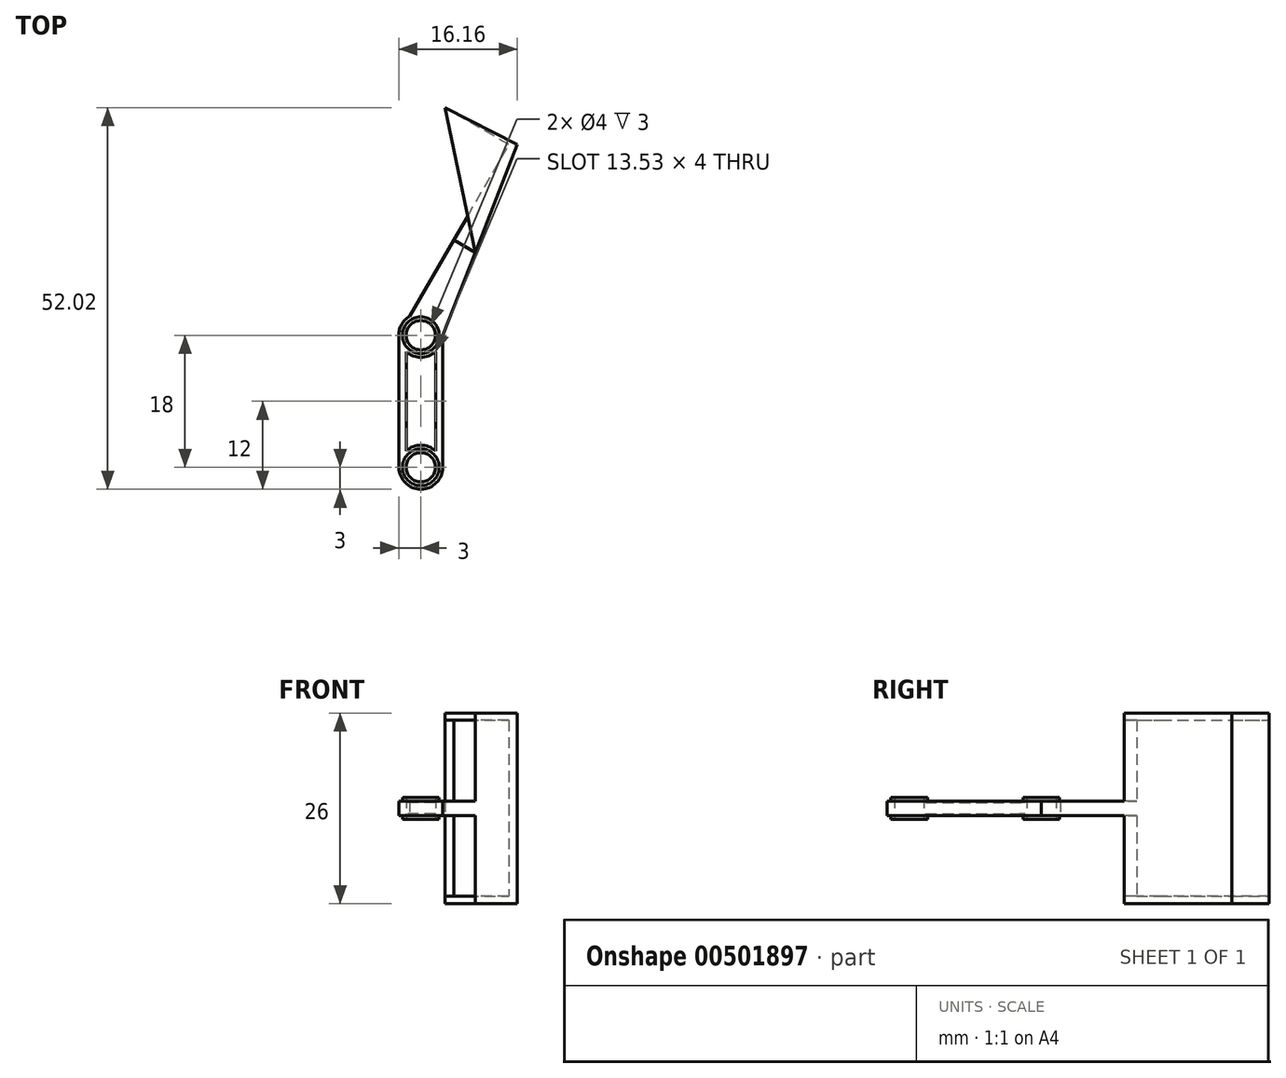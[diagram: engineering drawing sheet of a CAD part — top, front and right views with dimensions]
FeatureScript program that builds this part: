
annotation { "Feature Type Name" : "Feature", "Feature Type Description" : "" }
export const myFeature = defineFeature(function(context is Context, id is Id, definition is map)
    precondition{}
    {
        {
            var Q0;
            Q0=qCreatedBy(makeId("Front.planeOp"),FACE);
            var sketch = newSketch(context, id + "F0", { "sketchPlane" : qUnion([Q0])});
            skLineSegment(sketch, "E0.left", {"start": v(3, -1) * mm, "end": v(3, 1) * mm});
            skLineSegment(sketch, "E0.right", {"start": v(-3, -1) * mm, "end": v(-3, 1) * mm});
            skPoint(sketch, "E0.middle", {"position": v(0, 0) * mm});
            skLineSegment(sketch, "E1", {"start": v(-3, 1) * mm, "end": v(-2, 1) * mm});
            skLineSegment(sketch, "E2", {"start": v(-2, 1) * mm, "end": v(-2, 0.75) * mm});
            skLineSegment(sketch, "E3", {"start": v(-2, 0.75) * mm, "end": v(2, 0.75) * mm});
            skLineSegment(sketch, "E4", {"start": v(2, 0.75) * mm, "end": v(2, 1) * mm});
            skLineSegment(sketch, "E5", {"start": v(2, 1) * mm, "end": v(3, 1) * mm});
            skLineSegment(sketch, "E6", {"start": v(-3, -1) * mm, "end": v(-2, -1) * mm});
            skLineSegment(sketch, "E7", {"start": v(-2, -1) * mm, "end": v(-2, -0.75) * mm});
            skLineSegment(sketch, "E8", {"start": v(-2, -0.75) * mm, "end": v(2, -0.75) * mm});
            skLineSegment(sketch, "E9", {"start": v(2, -0.75) * mm, "end": v(2, -1) * mm});
            skLineSegment(sketch, "E10", {"start": v(2, -1) * mm, "end": v(3, -1) * mm});
            skSolve(sketch);
        }
        {
            var Q0;
            Q0=makeQuery(id+"F0.imprint","IMPRINT",FACE,{"disambiguationData":[TD([[makeQuery(id+"F0.imprint","IMPRINT",EDGE,{"derivedFrom":sQuery(id+"F0.wireOp",EDGE,"E0.left")}),1.0]])]});
            extrude(context, id + "F1", {"entities" : qUnion([Q0]), "endBound" : BoundingType.SYMMETRIC, "depth" : 18 * mm});
        }
        {
            var Q0;
            Q0=makeQuery(id+"F1.opExtrude","SWEPT_FACE",FACE,{"disambiguationData":[OSD([sQuery(id+"F0.wireOp",EDGE,"E8")])]});
            var sketch = newSketch(context, id + "F2", { "sketchPlane" : qUnion([Q0])});
            skCircle(sketch, "E11", {"center": v(0, 9) * mm, "radius": 2 * mm});
            skCircle(sketch, "E12", {"center": v(0, 9) * mm, "radius": 3 * mm});
            skCircle(sketch, "E13", {"center": v(0, -9) * mm, "radius": 2 * mm});
            skPoint(sketch, "E13.centerSnap0", {"position": v(0, -9) * mm});
            skCircle(sketch, "E14", {"center": v(0, -9) * mm, "radius": 3 * mm});
            skSolve(sketch);
        }
        {
            var Q0;
            {var subQ1=sQuery(id+"F0.wireOp",EDGE,"E8");var subQ2=makeQuery(id+"F1.opExtrude","CAP_EDGE",EDGE,{"disambiguationData":[OSD([subQ1])],"isStart":false});Q0=makeQuery(id+"F2.imprint","IMPRINT",FACE,{"disambiguationData":[TD([[makeQuery(id+"F2.imprint","IMPRINT",EDGE,{"derivedFrom":subQ2}),-1.0]])]});}
            extrude(context, id + "F3", {"entities" : qUnion([Q0]), "operationType" : NewBodyOperationType.REMOVE, "oppositeDirection" : true, "depth" : 2 * mm});
        }
        {
            var Q0;
            {var subQ1=sQuery(id+"F0.wireOp",EDGE,"E8");var subQ2=makeQuery(id+"F1.opExtrude","CAP_EDGE",EDGE,{"disambiguationData":[OSD([subQ1])],"isStart":true});Q0=makeQuery(id+"F2.imprint","IMPRINT",FACE,{"disambiguationData":[TD([[makeQuery(id+"F2.imprint","IMPRINT",EDGE,{"derivedFrom":subQ2}),1.0]])]});}
            extrude(context, id + "F4", {"entities" : qUnion([Q0]), "operationType" : NewBodyOperationType.REMOVE, "oppositeDirection" : true, "depth" : 2 * mm});
        }
        {
            var Q0;
            {var subQ1=sQuery(id+"F0.wireOp",EDGE,"E8");var subQ3=makeQuery(id+"F1.opExtrude","SWEPT_EDGE",EDGE,{"disambiguationData":[OSD([sQuery(id+"F0.wireOp",EDGE,"E7"),subQ1])]});var subQ7=sQuery(id+"F2.wireOp",EDGE,"E14");var subQ8=makeQuery(id+"F2.imprint","INTERSECT",VERTEX,{"derivedFrom":[subQ3,subQ7]});Q0=makeQuery(id+"F2.imprint","IMPRINT",FACE,{"disambiguationData":[TD([[makeQuery(id+"F2.imprint","IMPRINT",EDGE,{"disambiguationData":[TD([[subQ8,-1.0]])],"derivedFrom":subQ7}),1.0]])]});}
            var Q1;
            {var subQ1=sQuery(id+"F0.wireOp",EDGE,"E8");var subQ3=makeQuery(id+"F1.opExtrude","SWEPT_EDGE",EDGE,{"disambiguationData":[OSD([sQuery(id+"F0.wireOp",EDGE,"E7"),subQ1])]});var subQ7=sQuery(id+"F2.wireOp",EDGE,"E14");var subQ8=makeQuery(id+"F2.imprint","INTERSECT",VERTEX,{"derivedFrom":[subQ3,subQ7]});Q1=makeQuery(id+"F2.imprint","IMPRINT",FACE,{"disambiguationData":[TD([[makeQuery(id+"F2.imprint","IMPRINT",EDGE,{"disambiguationData":[TD([[subQ8,1.0]])],"derivedFrom":subQ7}),1.0]])]});}
            extrude(context, id + "F5", {"entities" : qUnion([Q0, Q1]), "operationType" : NewBodyOperationType.REMOVE, "oppositeDirection" : true, "depth" : 2 * mm});
        }
        {
            var Q0;
            {var subQ1=sQuery(id+"F0.wireOp",EDGE,"E8");var subQ3=makeQuery(id+"F1.opExtrude","SWEPT_EDGE",EDGE,{"disambiguationData":[OSD([sQuery(id+"F0.wireOp",EDGE,"E7"),subQ1])]});var subQ7=sQuery(id+"F2.wireOp",EDGE,"E14");var subQ8=makeQuery(id+"F2.imprint","INTERSECT",VERTEX,{"derivedFrom":[subQ3,subQ7]});Q0=makeQuery(id+"F2.imprint","IMPRINT",FACE,{"disambiguationData":[TD([[makeQuery(id+"F2.imprint","IMPRINT",EDGE,{"disambiguationData":[TD([[subQ8,-1.0]])],"derivedFrom":subQ7}),1.0]])]});}
            extrude(context, id + "F6", {"entities" : qUnion([Q0]), "operationType" : NewBodyOperationType.REMOVE, "oppositeDirection" : true, "depth" : 25 * mm});
        }
        {
            var Q0;
            {var subQ1=sQuery(id+"F0.wireOp",EDGE,"E8");var subQ3=makeQuery(id+"F1.opExtrude","SWEPT_EDGE",EDGE,{"disambiguationData":[OSD([sQuery(id+"F0.wireOp",EDGE,"E7"),subQ1])]});var subQ7=sQuery(id+"F2.wireOp",EDGE,"E14");var subQ8=makeQuery(id+"F2.imprint","INTERSECT",VERTEX,{"derivedFrom":[subQ3,subQ7]});Q0=makeQuery(id+"F2.imprint","IMPRINT",FACE,{"disambiguationData":[TD([[makeQuery(id+"F2.imprint","IMPRINT",EDGE,{"disambiguationData":[TD([[subQ8,-1.0]])],"derivedFrom":subQ7}),1.0]])]});}
            extrude(context, id + "F7", {"entities" : qUnion([Q0]), "operationType" : NewBodyOperationType.REMOVE, "oppositeDirection" : true, "depth" : 25 * mm});
        }
        {
            var Q0;
            {var subQ1=sQuery(id+"F0.wireOp",EDGE,"E8");var subQ3=makeQuery(id+"F1.opExtrude","SWEPT_EDGE",EDGE,{"disambiguationData":[OSD([sQuery(id+"F0.wireOp",EDGE,"E7"),subQ1])]});var subQ7=sQuery(id+"F2.wireOp",EDGE,"E14");var subQ8=makeQuery(id+"F2.imprint","INTERSECT",VERTEX,{"derivedFrom":[subQ3,subQ7]});Q0=makeQuery(id+"F2.imprint","IMPRINT",FACE,{"disambiguationData":[TD([[makeQuery(id+"F2.imprint","IMPRINT",EDGE,{"disambiguationData":[TD([[subQ8,-1.0]])],"derivedFrom":subQ7}),1.0]])]});}
            extrude(context, id + "F8", {"entities" : qUnion([Q0]), "operationType" : NewBodyOperationType.REMOVE, "oppositeDirection" : true, "depth" : 25 * mm});
        }
        {
            var Q0;
            {var subQ1=sQuery(id+"F0.wireOp",EDGE,"E8");var subQ3=makeQuery(id+"F1.opExtrude","SWEPT_EDGE",EDGE,{"disambiguationData":[OSD([sQuery(id+"F0.wireOp",EDGE,"E7"),subQ1])]});var subQ7=sQuery(id+"F2.wireOp",EDGE,"E14");var subQ8=makeQuery(id+"F2.imprint","INTERSECT",VERTEX,{"derivedFrom":[subQ3,subQ7]});Q0=makeQuery(id+"F2.imprint","IMPRINT",FACE,{"disambiguationData":[TD([[makeQuery(id+"F2.imprint","IMPRINT",EDGE,{"disambiguationData":[TD([[subQ8,-1.0]])],"derivedFrom":subQ7}),1.0]])]});}
            extrude(context, id + "F9", {"entities" : qUnion([Q0]), "operationType" : NewBodyOperationType.REMOVE, "depth" : 2 * mm});
        }
        {
            var Q0;
            {var subQ1=sQuery(id+"F0.wireOp",EDGE,"E8");var subQ3=makeQuery(id+"F1.opExtrude","SWEPT_EDGE",EDGE,{"disambiguationData":[OSD([sQuery(id+"F0.wireOp",EDGE,"E7"),subQ1])]});var subQ7=sQuery(id+"F2.wireOp",EDGE,"E12");var subQ8=makeQuery(id+"F2.imprint","INTERSECT",VERTEX,{"derivedFrom":[subQ3,subQ7]});Q0=makeQuery(id+"F2.imprint","IMPRINT",FACE,{"disambiguationData":[TD([[makeQuery(id+"F2.imprint","IMPRINT",EDGE,{"disambiguationData":[TD([[subQ8,1.0]])],"derivedFrom":subQ7}),1.0]])]});}
            var Q1;
            {var subQ1=sQuery(id+"F0.wireOp",EDGE,"E8");var subQ3=makeQuery(id+"F1.opExtrude","SWEPT_EDGE",EDGE,{"disambiguationData":[OSD([sQuery(id+"F0.wireOp",EDGE,"E7"),subQ1])]});var subQ7=sQuery(id+"F2.wireOp",EDGE,"E12");var subQ8=makeQuery(id+"F2.imprint","INTERSECT",VERTEX,{"derivedFrom":[subQ3,subQ7]});Q1=makeQuery(id+"F2.imprint","IMPRINT",FACE,{"disambiguationData":[TD([[makeQuery(id+"F2.imprint","IMPRINT",EDGE,{"disambiguationData":[TD([[subQ8,-1.0]])],"derivedFrom":subQ7}),1.0]])]});}
            extrude(context, id + "F10", {"entities" : qUnion([Q0, Q1]), "operationType" : NewBodyOperationType.REMOVE, "oppositeDirection" : true, "depth" : 2 * mm});
        }
        {
            var Q0;
            {var subQ1=sQuery(id+"F0.wireOp",EDGE,"E8");var subQ3=makeQuery(id+"F1.opExtrude","SWEPT_EDGE",EDGE,{"disambiguationData":[OSD([sQuery(id+"F0.wireOp",EDGE,"E7"),subQ1])]});var subQ7=sQuery(id+"F2.wireOp",EDGE,"E12");var subQ8=makeQuery(id+"F2.imprint","INTERSECT",VERTEX,{"derivedFrom":[subQ3,subQ7]});Q0=makeQuery(id+"F2.imprint","IMPRINT",FACE,{"disambiguationData":[TD([[makeQuery(id+"F2.imprint","IMPRINT",EDGE,{"disambiguationData":[TD([[subQ8,1.0]])],"derivedFrom":subQ7}),1.0]])]});}
            extrude(context, id + "F11", {"entities" : qUnion([Q0]), "operationType" : NewBodyOperationType.REMOVE, "depth" : 2 * mm});
        }
        {
            var Q0;
            {var subQ1=sQuery(id+"F0.wireOp",EDGE,"E8");var subQ3=makeQuery(id+"F1.opExtrude","SWEPT_EDGE",EDGE,{"disambiguationData":[OSD([sQuery(id+"F0.wireOp",EDGE,"E7"),subQ1])]});var subQ7=sQuery(id+"F2.wireOp",EDGE,"E14");var subQ8=makeQuery(id+"F2.imprint","INTERSECT",VERTEX,{"derivedFrom":[subQ3,subQ7]});Q0=makeQuery(id+"F2.imprint","IMPRINT",FACE,{"disambiguationData":[TD([[makeQuery(id+"F2.imprint","IMPRINT",EDGE,{"disambiguationData":[TD([[subQ8,1.0]])],"derivedFrom":subQ7}),1.0]])]});}
            var Q1;
            {var subQ1=sQuery(id+"F0.wireOp",EDGE,"E8");var subQ3=makeQuery(id+"F1.opExtrude","SWEPT_EDGE",EDGE,{"disambiguationData":[OSD([sQuery(id+"F0.wireOp",EDGE,"E7"),subQ1])]});var subQ7=sQuery(id+"F2.wireOp",EDGE,"E14");var subQ8=makeQuery(id+"F2.imprint","INTERSECT",VERTEX,{"derivedFrom":[subQ3,subQ7]});Q1=makeQuery(id+"F2.imprint","IMPRINT",FACE,{"disambiguationData":[TD([[makeQuery(id+"F2.imprint","IMPRINT",EDGE,{"disambiguationData":[TD([[subQ8,-1.0]])],"derivedFrom":subQ7}),1.0]])]});}
            var Q2;
            {var subQ1=sQuery(id+"F0.wireOp",EDGE,"E8");var subQ3=makeQuery(id+"F1.opExtrude","SWEPT_EDGE",EDGE,{"disambiguationData":[OSD([sQuery(id+"F0.wireOp",EDGE,"E7"),subQ1])]});var subQ7=sQuery(id+"F2.wireOp",EDGE,"E12");var subQ8=makeQuery(id+"F2.imprint","INTERSECT",VERTEX,{"derivedFrom":[subQ3,subQ7]});Q2=makeQuery(id+"F2.imprint","IMPRINT",FACE,{"disambiguationData":[TD([[makeQuery(id+"F2.imprint","IMPRINT",EDGE,{"disambiguationData":[TD([[subQ8,-1.0]])],"derivedFrom":subQ7}),1.0]])]});}
            var Q3;
            {var subQ1=sQuery(id+"F0.wireOp",EDGE,"E8");var subQ3=makeQuery(id+"F1.opExtrude","SWEPT_EDGE",EDGE,{"disambiguationData":[OSD([sQuery(id+"F0.wireOp",EDGE,"E7"),subQ1])]});var subQ7=sQuery(id+"F2.wireOp",EDGE,"E12");var subQ8=makeQuery(id+"F2.imprint","INTERSECT",VERTEX,{"derivedFrom":[subQ3,subQ7]});Q3=makeQuery(id+"F2.imprint","IMPRINT",FACE,{"disambiguationData":[TD([[makeQuery(id+"F2.imprint","IMPRINT",EDGE,{"disambiguationData":[TD([[subQ8,1.0]])],"derivedFrom":subQ7}),1.0]])]});}
            extrude(context, id + "F12", {"entities" : qUnion([Q0, Q1, Q2, Q3]), "operationType" : NewBodyOperationType.ADD, "oppositeDirection" : true, "depth" : 1.75 * mm});
        }
        {
            var Q0;
            {var subQ1=sQuery(id+"F0.wireOp",EDGE,"E8");var subQ3=makeQuery(id+"F1.opExtrude","SWEPT_EDGE",EDGE,{"disambiguationData":[OSD([sQuery(id+"F0.wireOp",EDGE,"E7"),subQ1])]});var subQ7=sQuery(id+"F2.wireOp",EDGE,"E14");var subQ8=makeQuery(id+"F2.imprint","INTERSECT",VERTEX,{"derivedFrom":[subQ3,subQ7]});Q0=makeQuery(id+"F2.imprint","IMPRINT",FACE,{"disambiguationData":[TD([[makeQuery(id+"F2.imprint","IMPRINT",EDGE,{"disambiguationData":[TD([[subQ8,1.0]])],"derivedFrom":subQ7}),1.0]])]});}
            var Q1;
            {var subQ1=sQuery(id+"F0.wireOp",EDGE,"E8");var subQ3=makeQuery(id+"F1.opExtrude","SWEPT_EDGE",EDGE,{"disambiguationData":[OSD([sQuery(id+"F0.wireOp",EDGE,"E7"),subQ1])]});var subQ7=sQuery(id+"F2.wireOp",EDGE,"E14");var subQ8=makeQuery(id+"F2.imprint","INTERSECT",VERTEX,{"derivedFrom":[subQ3,subQ7]});Q1=makeQuery(id+"F2.imprint","IMPRINT",FACE,{"disambiguationData":[TD([[makeQuery(id+"F2.imprint","IMPRINT",EDGE,{"disambiguationData":[TD([[subQ8,-1.0]])],"derivedFrom":subQ7}),1.0]])]});}
            var Q2;
            {var subQ1=sQuery(id+"F0.wireOp",EDGE,"E8");var subQ3=makeQuery(id+"F1.opExtrude","SWEPT_EDGE",EDGE,{"disambiguationData":[OSD([sQuery(id+"F0.wireOp",EDGE,"E7"),subQ1])]});var subQ7=sQuery(id+"F2.wireOp",EDGE,"E12");var subQ8=makeQuery(id+"F2.imprint","INTERSECT",VERTEX,{"derivedFrom":[subQ3,subQ7]});Q2=makeQuery(id+"F2.imprint","IMPRINT",FACE,{"disambiguationData":[TD([[makeQuery(id+"F2.imprint","IMPRINT",EDGE,{"disambiguationData":[TD([[subQ8,-1.0]])],"derivedFrom":subQ7}),1.0]])]});}
            var Q3;
            {var subQ1=sQuery(id+"F0.wireOp",EDGE,"E8");var subQ3=makeQuery(id+"F1.opExtrude","SWEPT_EDGE",EDGE,{"disambiguationData":[OSD([sQuery(id+"F0.wireOp",EDGE,"E7"),subQ1])]});var subQ7=sQuery(id+"F2.wireOp",EDGE,"E12");var subQ8=makeQuery(id+"F2.imprint","INTERSECT",VERTEX,{"derivedFrom":[subQ3,subQ7]});Q3=makeQuery(id+"F2.imprint","IMPRINT",FACE,{"disambiguationData":[TD([[makeQuery(id+"F2.imprint","IMPRINT",EDGE,{"disambiguationData":[TD([[subQ8,1.0]])],"derivedFrom":subQ7}),1.0]])]});}
            extrude(context, id + "F13", {"entities" : qUnion([Q0, Q1, Q2, Q3]), "operationType" : NewBodyOperationType.ADD, "depth" : .25 * mm});
        }
        {
            var Q0;
            Q0=makeQuery(id+"F13.boolean.opBoolean","MERGE",FACE,{"derivedFrom":[makeQuery(id+"F1.opExtrude","SWEPT_FACE",FACE,{"disambiguationData":[OSD([sQuery(id+"F0.wireOp",EDGE,"E6")])]}),makeQuery(id+"F1.opExtrude","SWEPT_FACE",FACE,{"disambiguationData":[OSD([sQuery(id+"F0.wireOp",EDGE,"E10")])]}),makeQuery(id+"F13.opExtrude","CAP_FACE",FACE,{"disambiguationData":[OSD([sQuery(id+"F2.wireOp",EDGE,"E11"),sQuery(id+"F2.wireOp",EDGE,"E12")])],"isStart":false}),makeQuery(id+"F13.opExtrude","CAP_FACE",FACE,{"disambiguationData":[OSD([sQuery(id+"F2.wireOp",EDGE,"E13"),sQuery(id+"F2.wireOp",EDGE,"E14")])],"isStart":false})]});
            var sketch = newSketch(context, id + "F14", { "sketchPlane" : qUnion([Q0])});
            skCircle(sketch, "E15", {"center": v(0, 9) * mm, "radius": 2 * mm});
            skCircle(sketch, "E16", {"center": v(0, 9) * mm, "radius": 2.5 * mm});
            skCircle(sketch, "E17", {"center": v(0, -9) * mm, "radius": 2 * mm});
            skCircle(sketch, "E18", {"center": v(0, -9) * mm, "radius": 2.5 * mm});
            skSolve(sketch);
        }
        {
            var Q0;
            Q0=makeQuery(id+"F14.imprint","IMPRINT",FACE,{"disambiguationData":[TD([[makeQuery(id+"F14.imprint","IMPRINT",EDGE,{"derivedFrom":sQuery(id+"F14.wireOp",EDGE,"E15")}),-1.0]])]});
            var Q1;
            Q1=makeQuery(id+"F14.imprint","IMPRINT",FACE,{"disambiguationData":[TD([[makeQuery(id+"F14.imprint","IMPRINT",EDGE,{"derivedFrom":sQuery(id+"F14.wireOp",EDGE,"E17")}),-1.0]])]});
            extrude(context, id + "F15", {"entities" : qUnion([Q0, Q1]), "operationType" : NewBodyOperationType.ADD, "depth" : .5 * mm});
        }
        {
            var Q0;
            Q0=makeQuery(id+"F12.boolean.opBoolean","MERGE",FACE,{"derivedFrom":[makeQuery(id+"F1.opExtrude","SWEPT_FACE",FACE,{"disambiguationData":[OSD([sQuery(id+"F0.wireOp",EDGE,"E1")])]}),makeQuery(id+"F1.opExtrude","SWEPT_FACE",FACE,{"disambiguationData":[OSD([sQuery(id+"F0.wireOp",EDGE,"E5")])]}),makeQuery(id+"F12.opExtrude","CAP_FACE",FACE,{"disambiguationData":[OSD([sQuery(id+"F2.wireOp",EDGE,"E11"),sQuery(id+"F2.wireOp",EDGE,"E12")])],"isStart":false}),makeQuery(id+"F12.opExtrude","CAP_FACE",FACE,{"disambiguationData":[OSD([sQuery(id+"F2.wireOp",EDGE,"E13"),sQuery(id+"F2.wireOp",EDGE,"E14")])],"isStart":false})]});
            var sketch = newSketch(context, id + "F16", { "sketchPlane" : qUnion([Q0])});
            skCircle(sketch, "E19", {"center": v(0, -9) * mm, "radius": 2 * mm});
            skCircle(sketch, "E20", {"center": v(0, -9) * mm, "radius": 2.5 * mm});
            skCircle(sketch, "E21", {"center": v(0, 9) * mm, "radius": 2 * mm});
            skCircle(sketch, "E22", {"center": v(0, 9) * mm, "radius": 2.5 * mm});
            skSolve(sketch);
        }
        {
            var Q0;
            Q0=makeQuery(id+"F16.imprint","IMPRINT",FACE,{"disambiguationData":[TD([[makeQuery(id+"F16.imprint","IMPRINT",EDGE,{"derivedFrom":sQuery(id+"F16.wireOp",EDGE,"E21")}),1.0]])]});
            var Q1;
            Q1=makeQuery(id+"F16.imprint","IMPRINT",FACE,{"disambiguationData":[TD([[makeQuery(id+"F16.imprint","IMPRINT",EDGE,{"derivedFrom":sQuery(id+"F16.wireOp",EDGE,"E19")}),1.0]])]});
            extrude(context, id + "F17", {"entities" : qUnion([Q0, Q1]), "operationType" : NewBodyOperationType.ADD, "depth" : .5 * mm});
        }
        {
            var Q0;
            Q0=qCreatedBy(makeId("Top.planeOp"),FACE);
            var sketch = newSketch(context, id + "F18", { "sketchPlane" : qUnion([Q0])});
            skLineSegment(sketch, "E23", {"start": v(0, 9) * mm, "end": v(-10.23, 14.9) * mm, "construction": true});
            skLineSegment(sketch, "E24", {"start": v(12, 34.98) * mm, "end": v(3.27, 40.02) * mm});
            skLineSegment(sketch, "E25", {"start": v(3.27, 40.02) * mm, "end": v(13.16, 34.98) * mm});
            skLineSegment(sketch, "E26", {"start": v(13.16, 34.98) * mm, "end": v(3, 9) * mm});
            skPoint(sketch, "E27", {"position": v(-3, 9) * mm});
            skPoint(sketch, "E28", {"position": v(-1.5, 11.6) * mm});
            skLineSegment(sketch, "E29.trimOffspring", {"start": v(-1.5, 11.6) * mm, "end": v(12, 34.98) * mm});
            skArc(sketch, "E30", {"start": v(3, 9) * mm, "mid": v(1.5, 11.6) * mm, "end": v(-1.5, 11.6) * mm});
            skPoint(sketch, "E31", {"position": v(4.5, 22) * mm});
            skLineSegment(sketch, "E32", {"start": v(4.5, 22) * mm, "end": v(7.42, 20.3) * mm});
            skSolve(sketch);
        }
        {
            var Q0;
            {var subQ0=sQuery(id+"F18.wireOp",EDGE,"E30");Q0=makeQuery(id+"F18.imprint","IMPRINT",FACE,{"disambiguationData":[TD([[makeQuery(id+"F18.imprint","IMPRINT",EDGE,{"derivedFrom":subQ0}),-1.0]])]});}
            extrude(context, id + "F19", {"entities" : qUnion([Q0]), "operationType" : NewBodyOperationType.ADD, "endBound" : BoundingType.SYMMETRIC, "depth" : 2 * mm});
        }
        {
            var Q0;
            {var subQ4=sQuery(id+"F18.wireOp",EDGE,"E24");Q0=makeQuery(id+"F18.imprint","IMPRINT",FACE,{"disambiguationData":[TD([[makeQuery(id+"F18.imprint","IMPRINT",EDGE,{"derivedFrom":subQ4}),-1.0]])]});}
            var Q1;
            Q1=qSketchRegion(id+"F23",true);
            extrude(context, id + "F20", {"entities" : qUnion([Q0, Q1]), "operationType" : NewBodyOperationType.ADD, "endBound" : BoundingType.SYMMETRIC, "depth" : 24 * mm});
        }
        {
            var Q0;
            Q0=makeQuery(id+"F20.opExtrude","CAP_FACE",FACE,{"disambiguationData":[OSD([sQuery(id+"F18.wireOp",EDGE,"E24"),sQuery(id+"F18.wireOp",EDGE,"E25"),sQuery(id+"F18.wireOp",EDGE,"E26"),sQuery(id+"F18.wireOp",EDGE,"E29.trimOffspring"),sQuery(id+"F18.wireOp",EDGE,"E32")])],"isStart":true});
            var sketch = newSketch(context, id + "F21", { "sketchPlane" : qUnion([Q0])});
            skLineSegment(sketch, "E33", {"start": v(7.42, -20.3) * mm, "end": v(13.16, -34.98) * mm});
            skLineSegment(sketch, "E34", {"start": v(13.16, -34.98) * mm, "end": v(3.27, -40.02) * mm});
            skLineSegment(sketch, "E35", {"start": v(3.27, -40.02) * mm, "end": v(7.42, -20.3) * mm});
            skSolve(sketch);
        }
        {
            var Q0;
            Q0=qSketchRegion(id+"F21",true);
            extrude(context, id + "F22", {"entities" : qUnion([Q0]), "operationType" : NewBodyOperationType.ADD, "depth" : 1 * mm});
        }
        {
            var Q0;
            Q0=makeQuery(id+"F20.opExtrude","CAP_FACE",FACE,{"disambiguationData":[OSD([sQuery(id+"F18.wireOp",EDGE,"E24"),sQuery(id+"F18.wireOp",EDGE,"E25"),sQuery(id+"F18.wireOp",EDGE,"E26"),sQuery(id+"F18.wireOp",EDGE,"E29.trimOffspring"),sQuery(id+"F18.wireOp",EDGE,"E32")])],"isStart":false});
            var sketch = newSketch(context, id + "F23", { "sketchPlane" : qUnion([Q0])});
            skLineSegment(sketch, "E36", {"start": v(7.42, 20.3) * mm, "end": v(3.27, 40.02) * mm});
            skLineSegment(sketch, "E37", {"start": v(3.27, 40.02) * mm, "end": v(13.16, 34.98) * mm});
            skLineSegment(sketch, "E38", {"start": v(13.16, 34.98) * mm, "end": v(7.42, 20.3) * mm});
            skSolve(sketch);
        }
        {
            var Q0;
            {var subQ1=makeQuery(id+"F20.opExtrude","CAP_EDGE",EDGE,{"disambiguationData":[OSD([sQuery(id+"F18.wireOp",EDGE,"E24")])],"isStart":false});Q0=makeQuery(id+"F23.imprint","IMPRINT",FACE,{"disambiguationData":[TD([[makeQuery(id+"F23.imprint","IMPRINT",EDGE,{"derivedFrom":subQ1}),1.0]])]});}
            var Q1;
            Q1=makeQuery(id+"F23.imprint","IMPRINT",FACE,{"disambiguationData":[TD([[makeQuery(id+"F23.imprint","IMPRINT",EDGE,{"derivedFrom":sQuery(id+"F23.wireOp",EDGE,"E37")}),-1.0]])]});
            extrude(context, id + "F24", {"entities" : qUnion([Q0, Q1]), "operationType" : NewBodyOperationType.ADD, "depth" : 1 * mm});
        }
    });
